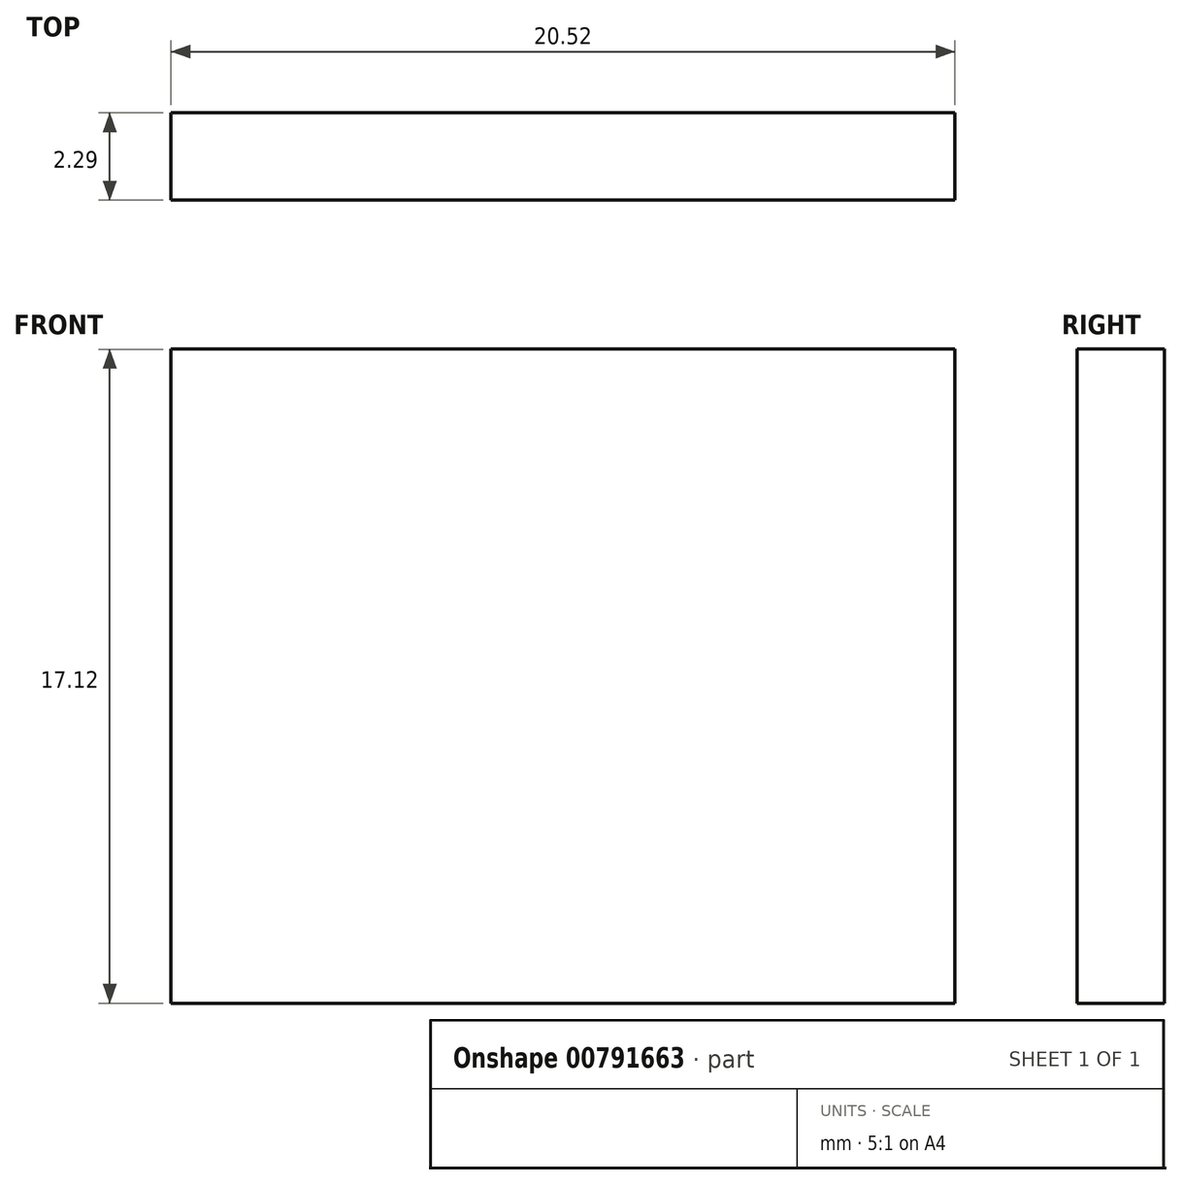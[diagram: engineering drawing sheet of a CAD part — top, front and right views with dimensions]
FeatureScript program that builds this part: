
annotation { "Feature Type Name" : "Feature", "Feature Type Description" : "" }
export const myFeature = defineFeature(function(context is Context, id is Id, definition is map)
    precondition{}
    {
        {
            var Q0;
            Q0=qCreatedBy(makeId("Front.planeOp"),FACE);
            var sketch = newSketch(context, id + "F0", { "sketchPlane" : qUnion([Q0])});
            skLineSegment(sketch, "E0.bottom", {"start": v(-51.64, 50.71) * mm, "end": v(-31.12, 50.71) * mm});
            skLineSegment(sketch, "E0.top", {"start": v(-51.64, 33.6) * mm, "end": v(-31.12, 33.6) * mm});
            skLineSegment(sketch, "E0.left", {"start": v(-51.64, 50.71) * mm, "end": v(-51.64, 33.6) * mm});
            skLineSegment(sketch, "E0.right", {"start": v(-31.12, 50.71) * mm, "end": v(-31.12, 33.6) * mm});
            skSolve(sketch);
        }
        {
            var Q0;
            Q0=makeQuery(id+"F0.imprint","IMPRINT",FACE,{"disambiguationData":[TD([[makeQuery(id+"F0.imprint","IMPRINT",EDGE,{"derivedFrom":sQuery(id+"F0.wireOp",EDGE,"E0.bottom")}),-1.0]])]});
            extrude(context, id + "F1", {"entities" : qUnion([Q0]), "depth" : 2.3 * mm, "offsetDistance" : 25.4 * mm});
        }
    });
